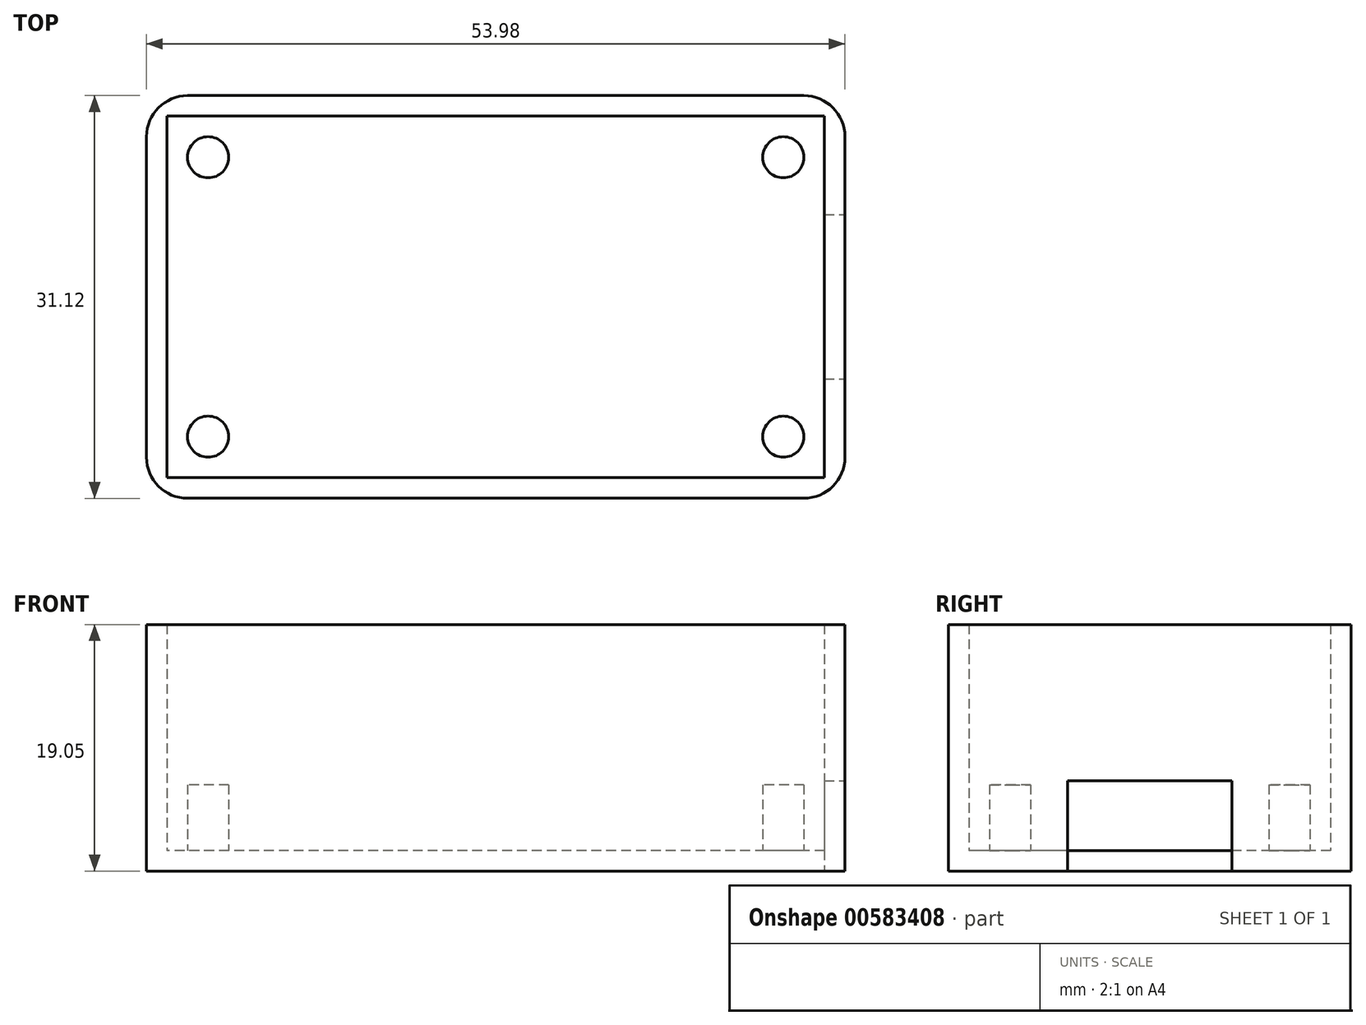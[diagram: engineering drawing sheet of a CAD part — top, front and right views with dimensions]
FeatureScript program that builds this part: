
annotation { "Feature Type Name" : "Feature", "Feature Type Description" : "" }
export const myFeature = defineFeature(function(context is Context, id is Id, definition is map)
    precondition{}
    {
        {
            var Q0;
            Q0=qCreatedBy(makeId("Top.planeOp"),FACE);
            var sketch = newSketch(context, id + "F0", { "sketchPlane" : qUnion([Q0])});
            skLineSegment(sketch, "E0.bottom", {"start": v(26.99, 15.56) * mm, "end": v(-26.99, 15.56) * mm});
            skLineSegment(sketch, "E0.top", {"start": v(26.99, -15.56) * mm, "end": v(-26.99, -15.56) * mm});
            skLineSegment(sketch, "E0.left", {"start": v(26.99, 15.56) * mm, "end": v(26.99, -15.56) * mm});
            skLineSegment(sketch, "E0.right", {"start": v(-26.99, 15.56) * mm, "end": v(-26.99, -15.56) * mm});
            skPoint(sketch, "E0.middle", {"position": v(0, 0) * mm});
            skSolve(sketch);
        }
        {
            var Q0;
            Q0 = qSketchRegion(id + "F0", true);
            extrude(context, id + "F1", {"entities" : qUnion([Q0]), "depth" : 19.05 * mm, "offsetDistance" : 25.4 * mm});
        }
        {
            var Q0;
            Q0=makeQuery(id+"F1.opExtrude","CAP_FACE",FACE,{"disambiguationData":[OSD([sQuery(id+"F0.wireOp",EDGE,"E0.bottom"),sQuery(id+"F0.wireOp",EDGE,"E0.top"),sQuery(id+"F0.wireOp",EDGE,"E0.left"),sQuery(id+"F0.wireOp",EDGE,"E0.right")])],"isStart":false});
            shell(context, id + "F2", {"entities" : qUnion([Q0]), "thickness" : 1.59 * mm});
        }
        {
            var Q0;
            Q0=makeQuery(id+"F2.opShell","OFFSET_FACE",FACE,{"disambiguationData":[OSD([sQuery(id+"F0.wireOp",EDGE,"E0.bottom"),sQuery(id+"F0.wireOp",EDGE,"E0.top"),sQuery(id+"F0.wireOp",EDGE,"E0.left"),sQuery(id+"F0.wireOp",EDGE,"E0.right")])]});
            var sketch = newSketch(context, id + "F3", { "sketchPlane" : qUnion([Q0])});
            skCircle(sketch, "E1", {"center": v(22.23, 10.8) * mm, "radius": 1.59 * mm});
            skPoint(sketch, "E1.first.point", {"position": v(21.39, 12.14) * mm});
            skPoint(sketch, "E1.second.point", {"position": v(23.53, 9.9) * mm});
            skPoint(sketch, "E1.third.point", {"position": v(22.36, 9.21) * mm});
            skCircle(sketch, "E2.MirrorC", {"center": v(22.23, -10.8) * mm, "radius": 1.59 * mm});
            skCircle(sketch, "E3.MirrorC", {"center": v(-22.23, 10.8) * mm, "radius": 1.59 * mm});
            skCircle(sketch, "E4.MirrorC", {"center": v(-22.23, -10.8) * mm, "radius": 1.59 * mm});
            skSolve(sketch);
        }
        {
            var Q0;
            Q0 = qSketchRegion(id + "F3", true);
            extrude(context, id + "F4", {"entities" : qUnion([Q0]), "operationType" : NewBodyOperationType.ADD, "depth" : 5.08 * mm, "offsetDistance" : 25.4 * mm});
        }
        {
            var Q0;
            Q0=makeQuery(id+"F1.opExtrude","SWEPT_FACE",FACE,{"disambiguationData":[OSD([sQuery(id+"F0.wireOp",EDGE,"E0.left")])]});
            var sketch = newSketch(context, id + "F5", { "sketchPlane" : qUnion([Q0])});
            skLineSegment(sketch, "E5.bottom", {"start": v(6.35, 6.98) * mm, "end": v(-6.35, 6.99) * mm});
            skLineSegment(sketch, "E5.top", {"start": v(6.35, -0.63) * mm, "end": v(-6.35, -0.63) * mm});
            skLineSegment(sketch, "E5.left", {"start": v(6.35, 6.99) * mm, "end": v(6.35, -0.63) * mm});
            skLineSegment(sketch, "E5.right", {"start": v(-6.35, 6.99) * mm, "end": v(-6.35, -0.63) * mm});
            skPoint(sketch, "E5.middle", {"position": v(0, 3.18) * mm});
            skSolve(sketch);
        }
        {
            var Q0;
            Q0 = qSketchRegion(id + "F5", true);
            extrude(context, id + "F6", {"entities" : qUnion([Q0]), "operationType" : NewBodyOperationType.REMOVE, "oppositeDirection" : true, "depth" : 1.59 * mm, "offsetDistance" : 25.4 * mm});
        }
        {
            var Q0;
            Q0=makeQuery(id+"F1.opExtrude","SWEPT_EDGE",EDGE,{"disambiguationData":[OSD([sQuery(id+"F0.wireOp",EDGE,"E0.top"),sQuery(id+"F0.wireOp",EDGE,"E0.left")])]});
            var Q1;
            Q1=makeQuery(id+"F1.opExtrude","SWEPT_EDGE",EDGE,{"disambiguationData":[OSD([sQuery(id+"F0.wireOp",EDGE,"E0.top"),sQuery(id+"F0.wireOp",EDGE,"E0.right")])]});
            var Q2;
            Q2=makeQuery(id+"F1.opExtrude","SWEPT_EDGE",EDGE,{"disambiguationData":[OSD([sQuery(id+"F0.wireOp",EDGE,"E0.bottom"),sQuery(id+"F0.wireOp",EDGE,"E0.right")])]});
            var Q3;
            Q3=makeQuery(id+"F1.opExtrude","SWEPT_EDGE",EDGE,{"disambiguationData":[OSD([sQuery(id+"F0.wireOp",EDGE,"E0.bottom"),sQuery(id+"F0.wireOp",EDGE,"E0.left")])]});
            fillet(context, id + "F7", {"entities" : qUnion([Q0, Q1, Q2, Q3]), "radius" : 3.17 * mm, "tangentPropagation" : true, "allowEdgeOverflow" : false});
        }
    });
